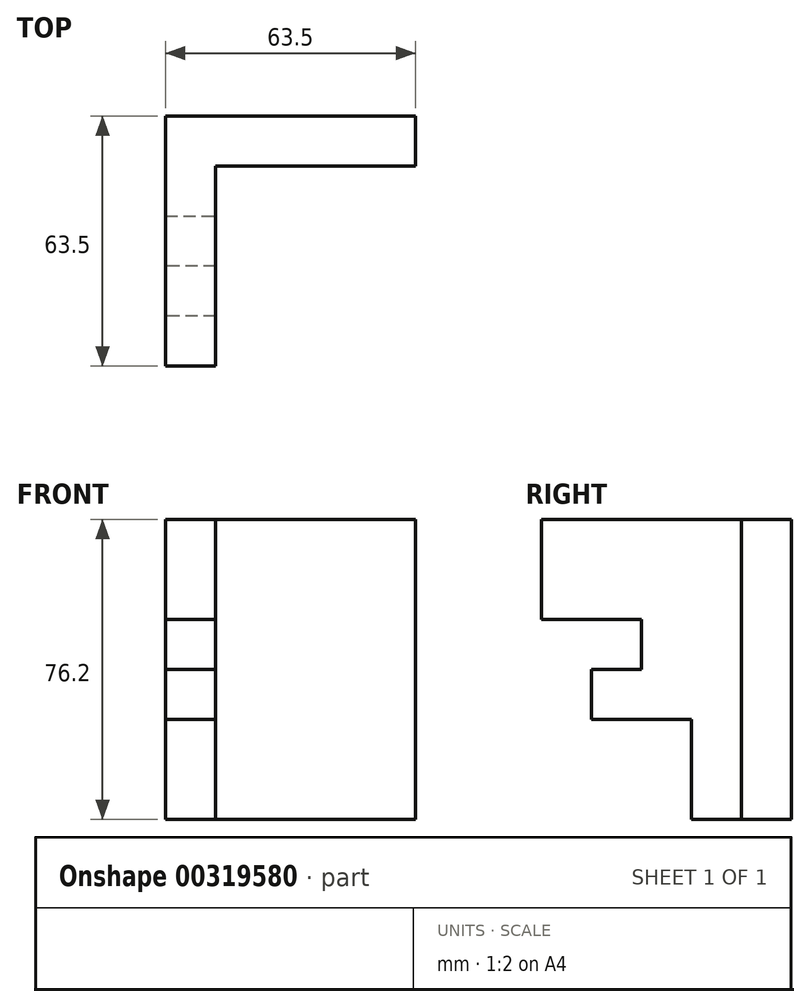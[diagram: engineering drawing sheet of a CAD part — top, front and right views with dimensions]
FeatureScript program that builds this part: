
annotation { "Feature Type Name" : "Feature", "Feature Type Description" : "" }
export const myFeature = defineFeature(function(context is Context, id is Id, definition is map)
    precondition{}
    {
        {
            var Q0;
            Q0=qCreatedBy(makeId("Front.planeOp"),FACE);
            var sketch = newSketch(context, id + "F0", { "sketchPlane" : qUnion([Q0])});
            skLineSegment(sketch, "E0", {"start": v(-28.86, -41) * mm, "end": v(34.64, -41) * mm});
            skLineSegment(sketch, "E1", {"start": v(34.64, -41) * mm, "end": v(34.64, 35.2) * mm});
            skLineSegment(sketch, "E2", {"start": v(34.64, 35.2) * mm, "end": v(-28.86, 35.2) * mm});
            skLineSegment(sketch, "E3", {"start": v(-28.86, 35.2) * mm, "end": v(-28.86, -41) * mm});
            skSolve(sketch);
        }
        {
            var Q0;
            Q0=makeQuery(id+"F0.imprint","IMPRINT",FACE,{"disambiguationData":[TD([[makeQuery(id+"F0.imprint","IMPRINT",EDGE,{"derivedFrom":sQuery(id+"F0.wireOp",EDGE,"E0")}),1.0]])]});
            extrude(context, id + "F1", {"entities" : qUnion([Q0]), "depth" : 12.7 * mm});
        }
        {
            var Q0;
            Q0=makeQuery(id+"F1.opExtrude","CAP_FACE",FACE,{"disambiguationData":[OSD([sQuery(id+"F0.wireOp",EDGE,"E0"),sQuery(id+"F0.wireOp",EDGE,"E1"),sQuery(id+"F0.wireOp",EDGE,"E2"),sQuery(id+"F0.wireOp",EDGE,"E3")])],"isStart":false});
            var sketch = newSketch(context, id + "F2", { "sketchPlane" : qUnion([Q0])});
            skLineSegment(sketch, "E4", {"start": v(-28.86, -41) * mm, "end": v(-16.16, -41) * mm});
            skLineSegment(sketch, "E5", {"start": v(-16.16, -41) * mm, "end": v(-16.16, -15.6) * mm});
            skLineSegment(sketch, "E6", {"start": v(-16.16, -15.6) * mm, "end": v(-28.86, -15.6) * mm});
            skLineSegment(sketch, "E7", {"start": v(-28.86, -15.6) * mm, "end": v(-28.86, -41) * mm});
            skSolve(sketch);
        }
        {
            var Q0;
            Q0=makeQuery(id+"F2.imprint","IMPRINT",FACE,{"disambiguationData":[TD([[makeQuery(id+"F2.imprint","IMPRINT",EDGE,{"derivedFrom":sQuery(id+"F2.wireOp",EDGE,"E4")}),1.0]])]});
            extrude(context, id + "F3", {"entities" : qUnion([Q0]), "operationType" : NewBodyOperationType.ADD, "depth" : 12.7 * mm});
        }
        {
            var Q0;
            Q0=makeQuery(id+"F1.opExtrude","CAP_FACE",FACE,{"disambiguationData":[OSD([sQuery(id+"F0.wireOp",EDGE,"E0"),sQuery(id+"F0.wireOp",EDGE,"E1"),sQuery(id+"F0.wireOp",EDGE,"E2"),sQuery(id+"F0.wireOp",EDGE,"E3")])],"isStart":false});
            var sketch = newSketch(context, id + "F4", { "sketchPlane" : qUnion([Q0])});
            skLineSegment(sketch, "E8", {"start": v(-28.86, -15.6) * mm, "end": v(-16.16, -15.6) * mm});
            skLineSegment(sketch, "E9", {"start": v(-16.16, -15.6) * mm, "end": v(-16.16, -2.9) * mm});
            skLineSegment(sketch, "E10", {"start": v(-16.16, -2.9) * mm, "end": v(-28.86, -2.9) * mm});
            skLineSegment(sketch, "E11", {"start": v(-28.86, -2.9) * mm, "end": v(-28.86, -15.6) * mm});
            skSolve(sketch);
        }
        {
            var Q0;
            Q0=makeQuery(id+"F4.imprint","IMPRINT",FACE,{"disambiguationData":[TD([[makeQuery(id+"F4.imprint","IMPRINT",EDGE,{"derivedFrom":sQuery(id+"F4.wireOp",EDGE,"E8")}),-1.0]])]});
            extrude(context, id + "F5", {"entities" : qUnion([Q0]), "operationType" : NewBodyOperationType.ADD, "depth" : 38.1 * mm});
        }
        {
            var Q0;
            Q0=makeQuery(id+"F1.opExtrude","CAP_FACE",FACE,{"disambiguationData":[OSD([sQuery(id+"F0.wireOp",EDGE,"E0"),sQuery(id+"F0.wireOp",EDGE,"E1"),sQuery(id+"F0.wireOp",EDGE,"E2"),sQuery(id+"F0.wireOp",EDGE,"E3")])],"isStart":false});
            var sketch = newSketch(context, id + "F6", { "sketchPlane" : qUnion([Q0])});
            skLineSegment(sketch, "E12", {"start": v(-28.86, -2.9) * mm, "end": v(-16.16, -2.9) * mm});
            skLineSegment(sketch, "E13", {"start": v(-16.16, -2.9) * mm, "end": v(-16.16, 9.8) * mm});
            skLineSegment(sketch, "E14", {"start": v(-16.16, 9.8) * mm, "end": v(-28.86, 9.8) * mm});
            skLineSegment(sketch, "E15", {"start": v(-28.86, 9.8) * mm, "end": v(-28.86, -2.9) * mm});
            skSolve(sketch);
        }
        {
            var Q0;
            Q0=makeQuery(id+"F6.imprint","IMPRINT",FACE,{"disambiguationData":[TD([[makeQuery(id+"F6.imprint","IMPRINT",EDGE,{"derivedFrom":sQuery(id+"F6.wireOp",EDGE,"E12")}),-1.0]])]});
            extrude(context, id + "F7", {"entities" : qUnion([Q0]), "operationType" : NewBodyOperationType.ADD, "depth" : 25.4 * mm});
        }
        {
            var Q0;
            Q0=makeQuery(id+"F1.opExtrude","CAP_FACE",FACE,{"disambiguationData":[OSD([sQuery(id+"F0.wireOp",EDGE,"E0"),sQuery(id+"F0.wireOp",EDGE,"E1"),sQuery(id+"F0.wireOp",EDGE,"E2"),sQuery(id+"F0.wireOp",EDGE,"E3")])],"isStart":false});
            var sketch = newSketch(context, id + "F8", { "sketchPlane" : qUnion([Q0])});
            skLineSegment(sketch, "E16", {"start": v(-28.86, 9.8) * mm, "end": v(-16.16, 9.8) * mm});
            skLineSegment(sketch, "E17", {"start": v(-16.16, 9.8) * mm, "end": v(-16.16, 35.2) * mm});
            skLineSegment(sketch, "E18", {"start": v(-16.16, 35.2) * mm, "end": v(-28.86, 35.2) * mm});
            skLineSegment(sketch, "E19", {"start": v(-28.86, 35.2) * mm, "end": v(-28.86, 9.8) * mm});
            skSolve(sketch);
        }
        {
            var Q0;
            Q0=makeQuery(id+"F8.imprint","IMPRINT",FACE,{"disambiguationData":[TD([[makeQuery(id+"F8.imprint","IMPRINT",EDGE,{"derivedFrom":sQuery(id+"F8.wireOp",EDGE,"E16")}),-1.0]])]});
            extrude(context, id + "F9", {"entities" : qUnion([Q0]), "operationType" : NewBodyOperationType.ADD, "depth" : 50.8 * mm});
        }
    });
